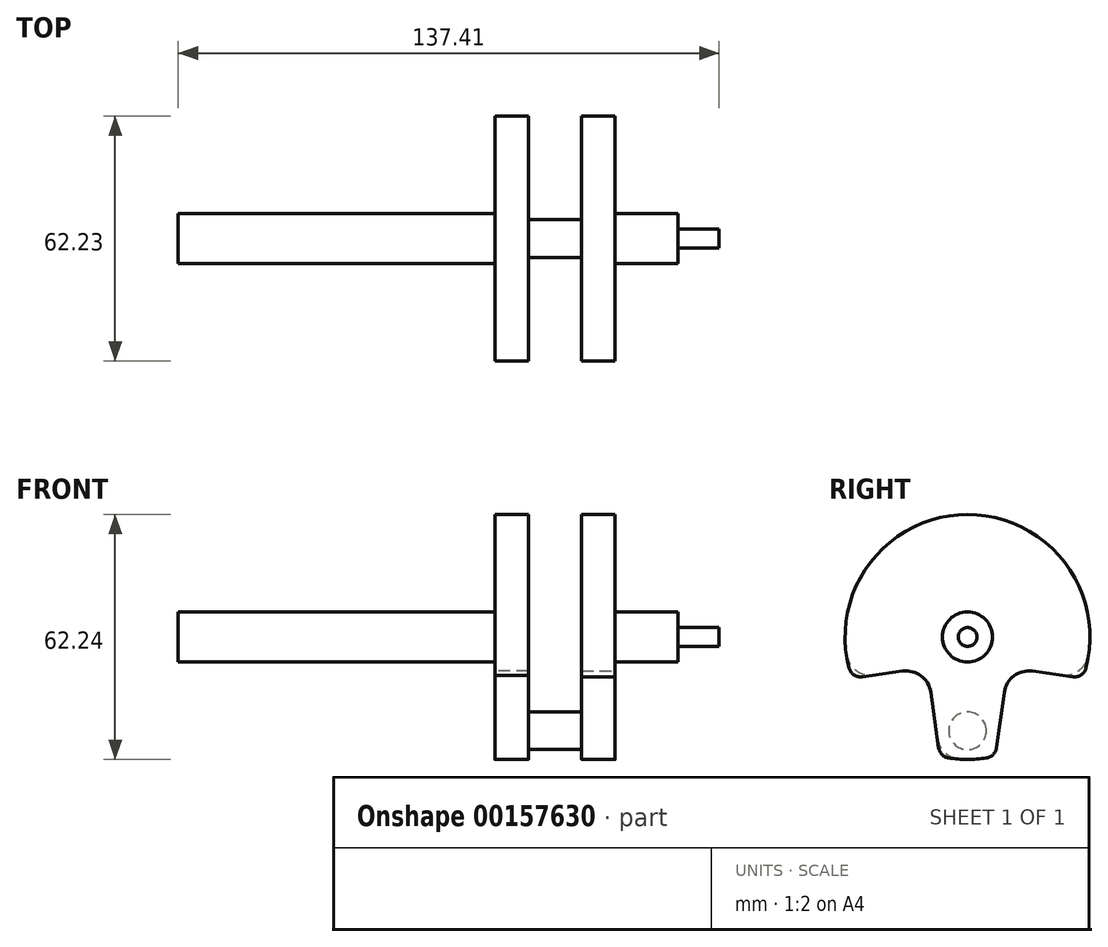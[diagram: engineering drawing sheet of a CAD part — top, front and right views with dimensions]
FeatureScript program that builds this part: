
annotation { "Feature Type Name" : "Feature", "Feature Type Description" : "" }
export const myFeature = defineFeature(function(context is Context, id is Id, definition is map)
    precondition{}
    {
        {
            var Q0;
            Q0=qCreatedBy(makeId("Right.planeOp"),FACE);
            var sketch = newSketch(context, id + "F0", { "sketchPlane" : qUnion([Q0])});
            skCircle(sketch, "E0", {"center": v(0, 0) * mm, "radius": 6.36 * mm});
            skPoint(sketch, "E1.center.orphan", {"position": v(0, -23.83) * mm});
            skPoint(sketch, "E2.visualSharp", {"position": v(10.19, -7.8) * mm});
            skPoint(sketch, "E3.visualSharp", {"position": v(-29.3, -10.48) * mm});
            skPoint(sketch, "E4.visualSharp", {"position": v(29.3, -10.48) * mm});
            skPoint(sketch, "E5.visualSharp", {"position": v(-10.2, -7.8) * mm});
            skCircle(sketch, "E6", {"center": v(0, -23.83) * mm, "radius": 4.78 * mm});
            skPoint(sketch, "E7.start.orphan", {"position": v(0, -31.12) * mm});
            skArc(sketch, "E8", {"start": v(-1.77, -31.06) * mm, "mid": v(1.5, -31.08) * mm, "end": v(4.77, -30.75) * mm});
            skArc(sketch, "E9.trimOffspring", {"start": v(30.82, -4.27) * mm, "mid": v(0, 31.12) * mm, "end": v(-30.82, -4.27) * mm});
            skLineSegment(sketch, "E10", {"start": v(-23.65, -9.69) * mm, "end": v(-16.5, -8.68) * mm});
            skLineSegment(sketch, "E11", {"start": v(-7.7, -25.6) * mm, "end": v(-9.32, -14.08) * mm});
            skLineSegment(sketch, "E12", {"start": v(16.47, -8.68) * mm, "end": v(23.65, -9.69) * mm});
            skLineSegment(sketch, "E13", {"start": v(7.32, -28.16) * mm, "end": v(9.3, -14.08) * mm});
            skPoint(sketch, "E14.start.orphan", {"position": v(0, -6.36) * mm});
            skArc(sketch, "E15.filletArc", {"start": v(-9.32, -14.08) * mm, "mid": v(-11.79, -9.9) * mm, "end": v(-16.5, -8.68) * mm});
            skArc(sketch, "E16.filletArc", {"start": v(-30.82, -4.27) * mm, "mid": v(-28.36, -8.47) * mm, "end": v(-23.65, -9.69) * mm});
            skArc(sketch, "E17.filletArc", {"start": v(23.65, -9.69) * mm, "mid": v(28.36, -8.47) * mm, "end": v(30.82, -4.27) * mm});
            skPoint(sketch, "E18.visualSharp", {"position": v(7.02, -30.31) * mm});
            skArc(sketch, "E18.filletArc", {"start": v(4.77, -30.75) * mm, "mid": v(6.48, -29.87) * mm, "end": v(7.32, -28.16) * mm});
            skPoint(sketch, "E19.visualSharp", {"position": v(-7.04, -30.3) * mm});
            skArc(sketch, "E19.filletArc", {"start": v(-7.7, -25.6) * mm, "mid": v(-5.71, -29.4) * mm, "end": v(-1.77, -31.06) * mm});
            skArc(sketch, "E20.filletArc", {"start": v(16.47, -8.68) * mm, "mid": v(11.77, -9.9) * mm, "end": v(9.3, -14.08) * mm});
            skSolve(sketch);
        }
        {
            var Q0;
            Q0=makeQuery(id+"F0.imprint","IMPRINT",FACE,{"disambiguationData":[TD([[makeQuery(id+"F0.imprint","IMPRINT",EDGE,{"derivedFrom":sQuery(id+"F0.wireOp",EDGE,"E0")}),-1.0]])]});
            var Q1;
            Q1=makeQuery(id+"F0.imprint","IMPRINT",FACE,{"disambiguationData":[TD([[makeQuery(id+"F0.imprint","IMPRINT",EDGE,{"derivedFrom":sQuery(id+"F0.wireOp",EDGE,"E0")}),1.0]])]});
            extrude(context, id + "F1", {"entities" : qUnion([Q0, Q1]), "depth" : 8.5 * mm});
        }
        {
            var Q0;
            Q0=makeQuery(id+"F0.imprint","IMPRINT",FACE,{"disambiguationData":[TD([[makeQuery(id+"F0.imprint","IMPRINT",EDGE,{"derivedFrom":sQuery(id+"F0.wireOp",EDGE,"E0")}),1.0]])]});
            extrude(context, id + "F2", {"entities" : qUnion([Q0]), "operationType" : NewBodyOperationType.ADD, "oppositeDirection" : true, "depth" : 80.44 * mm});
        }
        {
            var Q0;
            Q0=makeQuery(id+"F1.opExtrude","CAP_FACE",FACE,{"disambiguationData":[OSD([sQuery(id+"F0.wireOp",EDGE,"HB2RB507-PSp9-AoJ5-Lg5W-cgrda6hLqghh"),sQuery(id+"F0.wireOp",EDGE,"5dngh8rx-yReA-Kje8-LCi3-5LfM0G722O6K"),sQuery(id+"F0.wireOp",EDGE,"J8JSZUzQ-blgZ-UAfU-0OpU-OBjNJxEBiSRP"),sQuery(id+"F0.wireOp",EDGE,"E7"),sQuery(id+"F0.wireOp",EDGE,"KCazh3oR-FA4y-Wx0u-JUQt-vZ0FvvyvuGVR"),sQuery(id+"F0.wireOp",EDGE,"6IHcZjdQ-1Owb-Vqnl-Jesj-D2K21nGQ4lhP"),sQuery(id+"F0.wireOp",EDGE,"3390d13e-82a6-4ead-99fa-a2fe486d79d6.filletArc"),sQuery(id+"F0.wireOp",EDGE,"Q5gr6Njq-iQ6p-Q6l6-nTOV-pzhHfS1uZGks"),sQuery(id+"F0.wireOp",EDGE,"9776786b-44d9-46de-996b-b0988ea9cb89.filletArc"),sQuery(id+"F0.wireOp",EDGE,"E3.filletArc"),sQuery(id+"F0.wireOp",EDGE,"E4.filletArc"),sQuery(id+"F0.wireOp",EDGE,"E5.filletArc"),sQuery(id+"F0.wireOp",EDGE,"5hsjWpNG-mCCB-JqeH-vihm-ggomuKnmnca6"),sQuery(id+"F0.wireOp",EDGE,"GHEoGenM-6ubX-AgYc-3jiA-N8P0Jz4e3Q3f"),sQuery(id+"F0.wireOp",EDGE,"fda1fe06-c154-4a8a-9b2c-b4d9c88750a9.filletArc"),sQuery(id+"F0.wireOp",EDGE,"E6")])],"isStart":true});
            var sketch = newSketch(context, id + "F3", { "sketchPlane" : qUnion([Q0])});
            skCircle(sketch, "E21", {"center": v(0, -23.83) * mm, "radius": 4.78 * mm});
            skSolve(sketch);
        }
        {
            var Q0;
            Q0=makeQuery(id+"F3.imprint","IMPRINT",FACE,{"disambiguationData":[TD([[makeQuery(id+"F3.imprint","IMPRINT",EDGE,{"derivedFrom":sQuery(id+"F3.wireOp",EDGE,"E21")}),-1.0]])]});
            extrude(context, id + "F4", {"entities" : qUnion([Q0]), "operationType" : NewBodyOperationType.ADD, "oppositeDirection" : true, "depth" : 30.53 * mm});
        }
        {
            var Q0;
            Q0=makeQuery(id+"F4.opExtrude","CAP_FACE",FACE,{"disambiguationData":[OSD([sQuery(id+"F3.wireOp",EDGE,"E21")])],"isStart":false});
            var sketch = newSketch(context, id + "F5", { "sketchPlane" : qUnion([Q0])});
            skArc(sketch, "E22", {"start": v(30.1, -7.87) * mm, "mid": v(0, 31.12) * mm, "end": v(-30.1, -7.87) * mm});
            skLineSegment(sketch, "E23", {"start": v(-16.5, -8.68) * mm, "end": v(-26.73, -10.12) * mm});
            skLineSegment(sketch, "E24", {"start": v(16.5, -8.68) * mm, "end": v(26.73, -10.12) * mm});
            skLineSegment(sketch, "E25", {"start": v(9.32, -14.08) * mm, "end": v(7.8, -24.92) * mm});
            skLineSegment(sketch, "E26", {"start": v(-7.8, -24.92) * mm, "end": v(-9.32, -14.08) * mm});
            skLineSegment(sketch, "E27", {"start": v(7.8, -24.92) * mm, "end": v(7.34, -28.16) * mm});
            skLineSegment(sketch, "E28", {"start": v(-7.8, -24.92) * mm, "end": v(-7.34, -28.16) * mm});
            skArc(sketch, "E29.trimOffspring", {"start": v(-4.8, -30.74) * mm, "mid": v(0, -31.12) * mm, "end": v(4.8, -30.74) * mm});
            skPoint(sketch, "E30.visualSharp", {"position": v(-29.3, -10.48) * mm});
            skArc(sketch, "E30.filletArc", {"start": v(-30.1, -7.87) * mm, "mid": v(-28.84, -9.64) * mm, "end": v(-26.73, -10.12) * mm});
            skPoint(sketch, "E31.visualSharp", {"position": v(29.3, -10.48) * mm});
            skArc(sketch, "E31.filletArc", {"start": v(26.73, -10.12) * mm, "mid": v(28.84, -9.64) * mm, "end": v(30.1, -7.87) * mm});
            skPoint(sketch, "E32.visualSharp", {"position": v(7.04, -30.3) * mm});
            skArc(sketch, "E32.filletArc", {"start": v(4.8, -30.74) * mm, "mid": v(6.5, -29.87) * mm, "end": v(7.34, -28.16) * mm});
            skPoint(sketch, "E33.visualSharp", {"position": v(-7.04, -30.3) * mm});
            skArc(sketch, "E33.filletArc", {"start": v(-7.34, -28.16) * mm, "mid": v(-6.5, -29.87) * mm, "end": v(-4.8, -30.74) * mm});
            skPoint(sketch, "E34.visualSharp", {"position": v(-10.2, -7.8) * mm});
            skArc(sketch, "E34.filletArc", {"start": v(-9.32, -14.08) * mm, "mid": v(-11.79, -9.9) * mm, "end": v(-16.5, -8.68) * mm});
            skPoint(sketch, "E35.visualSharp", {"position": v(10.2, -7.8) * mm});
            skArc(sketch, "E35.filletArc", {"start": v(16.5, -8.68) * mm, "mid": v(11.79, -9.9) * mm, "end": v(9.32, -14.08) * mm});
            skPoint(sketch, "E36.orphan", {"position": v(0, -6.36) * mm});
            skCircle(sketch, "E37", {"center": v(0, 0) * mm, "radius": 6.36 * mm});
            skPoint(sketch, "E38.center.orphan", {"position": v(0, -23.83) * mm});
            skSolve(sketch);
        }
        {
            var Q0;
            Q0=makeQuery(id+"F5.imprint","IMPRINT",FACE,{"disambiguationData":[TD([[makeQuery(id+"F5.imprint","IMPRINT",EDGE,{"derivedFrom":sQuery(id+"F5.wireOp",EDGE,"E22")}),1.0]])]});
            extrude(context, id + "F6", {"entities" : qUnion([Q0]), "operationType" : NewBodyOperationType.ADD, "oppositeDirection" : true, "depth" : 8.5 * mm});
        }
        {
            var Q0;
            Q0=makeQuery(id+"F6.opExtrude","CAP_FACE",FACE,{"disambiguationData":[OSD([sQuery(id+"F3.wireOp",EDGE,"E21"),sQuery(id+"F5.wireOp",EDGE,"E22"),sQuery(id+"F5.wireOp",EDGE,"E23"),sQuery(id+"F5.wireOp",EDGE,"E24"),sQuery(id+"F5.wireOp",EDGE,"E25"),sQuery(id+"F5.wireOp",EDGE,"E26"),sQuery(id+"F5.wireOp",EDGE,"E27"),sQuery(id+"F5.wireOp",EDGE,"E28"),sQuery(id+"F5.wireOp",EDGE,"E29.trimOffspring"),sQuery(id+"F5.wireOp",EDGE,"E30.filletArc"),sQuery(id+"F5.wireOp",EDGE,"E31.filletArc"),sQuery(id+"F5.wireOp",EDGE,"E32.filletArc"),sQuery(id+"F5.wireOp",EDGE,"E33.filletArc"),sQuery(id+"F5.wireOp",EDGE,"E34.filletArc"),sQuery(id+"F5.wireOp",EDGE,"E35.filletArc"),sQuery(id+"F5.wireOp",EDGE,"E37")])],"isStart":false});
            var sketch = newSketch(context, id + "F7", { "sketchPlane" : qUnion([Q0])});
            skCircle(sketch, "E39", {"center": v(0, 0) * mm, "radius": 6.36 * mm});
            skSolve(sketch);
        }
        {
            var Q0;
            Q0=makeQuery(id+"F7.imprint","IMPRINT",FACE,{"disambiguationData":[TD([[makeQuery(id+"F7.imprint","IMPRINT",EDGE,{"derivedFrom":sQuery(id+"F7.wireOp",EDGE,"E39")}),-1.0]])]});
            extrude(context, id + "F8", {"entities" : qUnion([Q0]), "operationType" : NewBodyOperationType.ADD, "oppositeDirection" : true, "depth" : 24.54 * mm});
        }
        {
            var Q0;
            Q0=makeQuery(id+"F8.opExtrude","CAP_FACE",FACE,{"disambiguationData":[OSD([sQuery(id+"F7.wireOp",EDGE,"E39")])],"isStart":false});
            var sketch = newSketch(context, id + "F9", { "sketchPlane" : qUnion([Q0])});
            skCircle(sketch, "E40", {"center": v(0, 0) * mm, "radius": 2.38 * mm});
            skSolve(sketch);
        }
        {
            var Q0;
            Q0=makeQuery(id+"F9.imprint","IMPRINT",FACE,{"disambiguationData":[TD([[makeQuery(id+"F9.imprint","IMPRINT",EDGE,{"derivedFrom":sQuery(id+"F9.wireOp",EDGE,"E40")}),1.0]])]});
            extrude(context, id + "F10", {"entities" : qUnion([Q0]), "operationType" : NewBodyOperationType.ADD, "depth" : 10.4 * mm});
        }
    });
